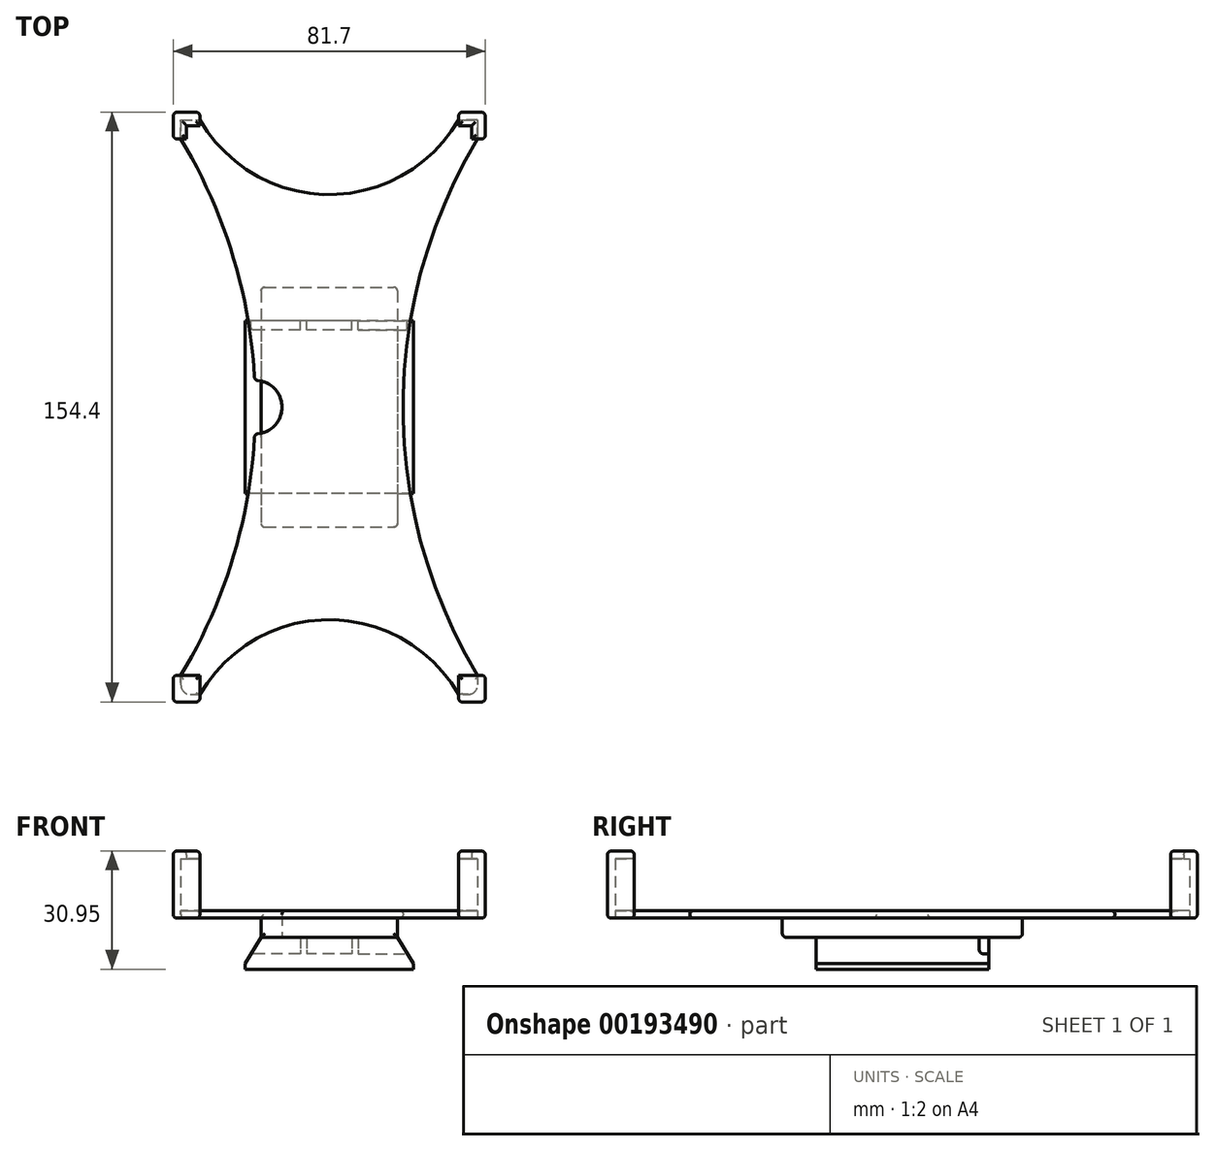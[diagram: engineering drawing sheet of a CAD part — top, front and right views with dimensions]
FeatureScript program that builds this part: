
annotation { "Feature Type Name" : "Feature", "Feature Type Description" : "" }
export const myFeature = defineFeature(function(context is Context, id is Id, definition is map)
    precondition{}
    {
        {
            var Q0;
            Q0=qCreatedBy(makeId("Top.planeOp"),FACE);
            var sketch = newSketch(context, id + "F0", { "sketchPlane" : qUnion([Q0])});
            skLineSegment(sketch, "E0.bottom", {"start": v(-38.85, 75.2) * mm, "end": v(-33.85, 75.2) * mm});
            skLineSegment(sketch, "E0.top", {"start": v(-38.85, -75.2) * mm, "end": v(-33.85, -75.2) * mm});
            skLineSegment(sketch, "E0.left", {"start": v(-38.85, 75.2) * mm, "end": v(-38.85, 70.2) * mm});
            skLineSegment(sketch, "E0.right", {"start": v(38.85, 75.2) * mm, "end": v(38.85, 70.2) * mm});
            skLineSegment(sketch, "E1", {"start": v(-38.85, 75.2) * mm, "end": v(38.85, -75.2) * mm, "construction": true});
            skArc(sketch, "E2", {"start": v(-33.85, 75.2) * mm, "mid": v(0, 55.65) * mm, "end": v(33.85, 75.2) * mm});
            skArc(sketch, "E3", {"start": v(-38.85, -70.2) * mm, "mid": v(-25.3, -39.79) * mm, "end": v(-19.53, -7) * mm});
            skArc(sketch, "E4.MirrorCS", {"start": v(38.85, -70.2) * mm, "mid": v(19.35, 0) * mm, "end": v(38.85, 70.2) * mm});
            skArc(sketch, "E5.MirrorCS", {"start": v(-33.85, -75.2) * mm, "mid": v(0, -55.65) * mm, "end": v(33.85, -75.2) * mm});
            skArc(sketch, "E6", {"start": v(-19.53, -7) * mm, "mid": v(-12.35, 0) * mm, "end": v(-19.53, 7) * mm});
            skArc(sketch, "E7.trimOffspring", {"start": v(-19.53, 7) * mm, "mid": v(-25.3, 39.79) * mm, "end": v(-38.85, 70.2) * mm});
            skLineSegment(sketch, "E8.bottom", {"start": v(-25.25, 66.5) * mm, "end": v(25.25, 66.5) * mm, "construction": true});
            skLineSegment(sketch, "E8.top", {"start": v(-25.25, 64.9) * mm, "end": v(25.25, 64.9) * mm, "construction": true});
            skLineSegment(sketch, "E8.left", {"start": v(-25.25, 66.5) * mm, "end": v(-25.25, 64.9) * mm, "construction": true});
            skLineSegment(sketch, "E8.right", {"start": v(25.25, 66.5) * mm, "end": v(25.25, 64.9) * mm, "construction": true});
            skLineSegment(sketch, "E9.trimOffspring", {"start": v(33.85, 75.2) * mm, "end": v(38.85, 75.2) * mm});
            skLineSegment(sketch, "E10.trimOffspring", {"start": v(-38.85, -70.2) * mm, "end": v(-38.85, -75.2) * mm});
            skLineSegment(sketch, "E11.trimOffspring", {"start": v(38.85, -70.2) * mm, "end": v(38.85, -75.2) * mm});
            skLineSegment(sketch, "E12.trimOffspring", {"start": v(33.85, -75.2) * mm, "end": v(38.85, -75.2) * mm});
            skSolve(sketch);
        }
        {
            var Q0;
            Q0 = qSketchRegion(id + "F0", true);
            extrude(context, id + "F1", {"entities" : qUnion([Q0]), "depth" : 2 * mm});
        }
        {
            var Q0;
            Q0=qCreatedBy(makeId("Top.planeOp"),FACE);
            var sketch = newSketch(context, id + "F2", { "sketchPlane" : qUnion([Q0])});
            skLineSegment(sketch, "E13", {"start": v(-33.85, 75.2) * mm, "end": v(-33.85, 77.2) * mm});
            skLineSegment(sketch, "E14", {"start": v(-33.85, 77.2) * mm, "end": v(-40.85, 77.2) * mm});
            skLineSegment(sketch, "E15", {"start": v(-40.85, 77.2) * mm, "end": v(-40.85, 70.2) * mm});
            skLineSegment(sketch, "E16", {"start": v(-40.85, 70.2) * mm, "end": v(-38.85, 70.2) * mm});
            skLineSegment(sketch, "E17", {"start": v(-38.85, 70.2) * mm, "end": v(-38.85, 75.2) * mm});
            skLineSegment(sketch, "E18", {"start": v(-38.85, 75.2) * mm, "end": v(-33.85, 75.2) * mm});
            skLineSegment(sketch, "E19.MirrorCS", {"start": v(40.85, 77.2) * mm, "end": v(40.85, 70.2) * mm});
            skLineSegment(sketch, "E20.MirrorCS", {"start": v(33.85, 77.2) * mm, "end": v(40.85, 77.2) * mm});
            skLineSegment(sketch, "E21.MirrorCS", {"start": v(40.85, 70.2) * mm, "end": v(38.85, 70.2) * mm});
            skLineSegment(sketch, "E22.MirrorCS", {"start": v(38.85, 75.2) * mm, "end": v(33.85, 75.2) * mm});
            skLineSegment(sketch, "E23.MirrorCS", {"start": v(38.85, 70.2) * mm, "end": v(38.85, 75.2) * mm});
            skLineSegment(sketch, "E24.MirrorCS", {"start": v(33.85, 75.2) * mm, "end": v(33.85, 77.2) * mm});
            skLineSegment(sketch, "E25.MirrorCS", {"start": v(33.85, -75.2) * mm, "end": v(33.85, -77.2) * mm});
            skLineSegment(sketch, "E26.MirrorCS", {"start": v(40.85, -70.2) * mm, "end": v(38.85, -70.2) * mm});
            skLineSegment(sketch, "E27.MirrorCS", {"start": v(-33.85, -75.2) * mm, "end": v(-33.85, -77.2) * mm});
            skLineSegment(sketch, "E28.MirrorCS", {"start": v(-40.85, -70.2) * mm, "end": v(-38.85, -70.2) * mm});
            skLineSegment(sketch, "E29.MirrorCS", {"start": v(38.85, -70.2) * mm, "end": v(38.85, -75.2) * mm});
            skLineSegment(sketch, "E30.MirrorCS", {"start": v(38.85, -75.2) * mm, "end": v(33.85, -75.2) * mm});
            skLineSegment(sketch, "E31.MirrorCS", {"start": v(33.85, -77.2) * mm, "end": v(40.85, -77.2) * mm});
            skLineSegment(sketch, "E32.MirrorCS", {"start": v(40.85, -77.2) * mm, "end": v(40.85, -70.2) * mm});
            skLineSegment(sketch, "E33.MirrorCS", {"start": v(-38.85, -75.2) * mm, "end": v(-33.85, -75.2) * mm});
            skLineSegment(sketch, "E34.MirrorCS", {"start": v(-38.85, -70.2) * mm, "end": v(-38.85, -75.2) * mm});
            skLineSegment(sketch, "E35.MirrorCS", {"start": v(-33.85, -77.2) * mm, "end": v(-40.85, -77.2) * mm});
            skLineSegment(sketch, "E36.MirrorCS", {"start": v(-40.85, -77.2) * mm, "end": v(-40.85, -70.2) * mm});
            skSolve(sketch);
        }
        {
            var Q0;
            Q0 = qSketchRegion(id + "F2", true);
            extrude(context, id + "F3", {"entities" : qUnion([Q0]), "operationType" : NewBodyOperationType.ADD, "depth" : (13.6 + 2) * mm});
        }
        {
            var Q0;
            Q0=makeQuery(id+"F3.opExtrude","CAP_FACE",FACE,{"disambiguationData":[OSD([sQuery(id+"F2.wireOp",EDGE,"E13"),sQuery(id+"F2.wireOp",EDGE,"E14"),sQuery(id+"F2.wireOp",EDGE,"E15"),sQuery(id+"F2.wireOp",EDGE,"E16"),sQuery(id+"F2.wireOp",EDGE,"E17"),sQuery(id+"F2.wireOp",EDGE,"E18")])],"isStart":false});
            var sketch = newSketch(context, id + "F4", { "sketchPlane" : qUnion([Q0])});
            skLineSegment(sketch, "E37.bottom", {"start": v(-40.85, -77.2) * mm, "end": v(-33.85, -77.2) * mm});
            skLineSegment(sketch, "E37.top", {"start": v(-40.85, -70.2) * mm, "end": v(-33.85, -70.2) * mm});
            skLineSegment(sketch, "E37.left", {"start": v(-40.85, -77.2) * mm, "end": v(-40.85, -70.2) * mm});
            skLineSegment(sketch, "E37.right", {"start": v(-33.85, -77.2) * mm, "end": v(-33.85, -70.2) * mm});
            skLineSegment(sketch, "E38", {"start": v(-40.85, 77.2) * mm, "end": v(-33.85, 77.2) * mm});
            skLineSegment(sketch, "E39", {"start": v(-33.85, 77.2) * mm, "end": v(-33.85, 73.7) * mm});
            skLineSegment(sketch, "E40", {"start": v(-33.85, 73.7) * mm, "end": v(-37.35, 73.7) * mm});
            skLineSegment(sketch, "E41", {"start": v(-37.35, 73.7) * mm, "end": v(-37.35, 70.2) * mm});
            skLineSegment(sketch, "E42", {"start": v(-37.35, 70.2) * mm, "end": v(-40.85, 70.2) * mm});
            skLineSegment(sketch, "E43", {"start": v(-40.85, 70.2) * mm, "end": v(-40.85, 77.2) * mm});
            skLineSegment(sketch, "E44.MirrorCS", {"start": v(33.85, 77.2) * mm, "end": v(33.85, 73.7) * mm});
            skLineSegment(sketch, "E45.MirrorCS", {"start": v(37.35, 70.2) * mm, "end": v(40.85, 70.2) * mm});
            skLineSegment(sketch, "E46.MirrorCS", {"start": v(33.85, 73.7) * mm, "end": v(37.35, 73.7) * mm});
            skLineSegment(sketch, "E47.MirrorCS", {"start": v(37.35, 73.7) * mm, "end": v(37.35, 70.2) * mm});
            skLineSegment(sketch, "E48.MirrorCS", {"start": v(40.85, -77.2) * mm, "end": v(40.85, -70.2) * mm});
            skLineSegment(sketch, "E49.MirrorCS", {"start": v(40.85, -70.2) * mm, "end": v(33.85, -70.2) * mm});
            skLineSegment(sketch, "E50.MirrorCS", {"start": v(40.85, 70.2) * mm, "end": v(40.85, 77.2) * mm});
            skLineSegment(sketch, "E51.MirrorCS", {"start": v(40.85, -77.2) * mm, "end": v(33.85, -77.2) * mm});
            skLineSegment(sketch, "E52.MirrorCS", {"start": v(40.85, 77.2) * mm, "end": v(33.85, 77.2) * mm});
            skLineSegment(sketch, "E53.MirrorCS", {"start": v(33.85, -77.2) * mm, "end": v(33.85, -70.2) * mm});
            skSolve(sketch);
        }
        {
            var Q0;
            Q0 = qSketchRegion(id + "F4", true);
            extrude(context, id + "F5", {"entities" : qUnion([Q0]), "operationType" : NewBodyOperationType.ADD, "depth" : 2 * mm});
        }
        {
            var Q0;
            Q0=qCreatedBy(makeId("Top.planeOp"),FACE);
            var sketch = newSketch(context, id + "F6", { "sketchPlane" : qUnion([Q0])});
            skLineSegment(sketch, "E54.bottom", {"start": v(-17.85, 31.43) * mm, "end": v(17.85, 31.43) * mm});
            skLineSegment(sketch, "E54.top", {"start": v(-17.85, -31.42) * mm, "end": v(17.85, -31.42) * mm});
            skLineSegment(sketch, "E54.left", {"start": v(-17.85, 31.43) * mm, "end": v(-17.85, 6.84) * mm});
            skLineSegment(sketch, "E54.right", {"start": v(17.85, 31.43) * mm, "end": v(17.85, -31.42) * mm});
            skLineSegment(sketch, "E55", {"start": v(-17.85, 31.43) * mm, "end": v(17.85, -31.43) * mm, "construction": true});
            skArc(sketch, "E56", {"start": v(-17.85, -6.84) * mm, "mid": v(-12.35, 0) * mm, "end": v(-17.85, 6.84) * mm});
            skLineSegment(sketch, "E57.trimOffspring", {"start": v(-17.85, -6.84) * mm, "end": v(-17.85, -31.42) * mm});
            skSolve(sketch);
        }
        {
            var Q0;
            Q0 = qSketchRegion(id + "F6", true);
            extrude(context, id + "F7", {"entities" : qUnion([Q0]), "operationType" : NewBodyOperationType.ADD, "oppositeDirection" : true, "depth" : 5 * mm});
        }
        {
            var Q0;
            Q0=makeQuery(id+"F7.opExtrude","CAP_FACE",FACE,{"disambiguationData":[OSD([sQuery(id+"F6.wireOp",EDGE,"E54.bottom"),sQuery(id+"F6.wireOp",EDGE,"E54.top"),sQuery(id+"F6.wireOp",EDGE,"E54.left"),sQuery(id+"F6.wireOp",EDGE,"E54.right"),sQuery(id+"F6.wireOp",EDGE,"E56"),sQuery(id+"F6.wireOp",EDGE,"E57.trimOffspring")])],"isStart":false});
            var sketch = newSketch(context, id + "F8", { "sketchPlane" : qUnion([Q0])});
            skLineSegment(sketch, "E58.bottom", {"start": v(17.85, -22.62) * mm, "end": v(-17.85, -22.62) * mm});
            skLineSegment(sketch, "E58.top", {"start": v(17.85, 22.62) * mm, "end": v(-17.85, 22.62) * mm});
            skLineSegment(sketch, "E58.left", {"start": v(17.85, -22.62) * mm, "end": v(17.85, 22.62) * mm});
            skLineSegment(sketch, "E58.right", {"start": v(-17.85, -22.62) * mm, "end": v(-17.85, 22.62) * mm});
            skPoint(sketch, "E58.middle", {"position": v(0, 0) * mm});
            skSolve(sketch);
        }
        {
            var Q0;
            {var subQ2=sQuery(id+"F8.wireOp",EDGE,"E58.bottom");Q0=makeQuery(id+"F8.imprint","IMPRINT",FACE,{"disambiguationData":[TD([[makeQuery(id+"F8.imprint","IMPRINT",EDGE,{"derivedFrom":subQ2}),-1.0]])]});}
            cPlane(context, id + "F9", {"entities" : qUnion([Q0]), "cplaneType" : CPlaneType.OFFSET, "offset" : 6.85 * mm, "width" : 150 * mm, "height" : 150 * mm});
        }
        {
            var Q0;
            Q0=qCreatedBy(id+"F9.planeOp",FACE);
            var sketch = newSketch(context, id + "F10", { "sketchPlane" : qUnion([Q0])});
            skLineSegment(sketch, "E59.bottom", {"start": v(22, -22.62) * mm, "end": v(-22, -22.62) * mm});
            skLineSegment(sketch, "E59.top", {"start": v(22, 22.62) * mm, "end": v(-22, 22.62) * mm});
            skLineSegment(sketch, "E59.left", {"start": v(22, -22.62) * mm, "end": v(22, 22.62) * mm});
            skLineSegment(sketch, "E59.right", {"start": v(-22, -22.62) * mm, "end": v(-22, 22.62) * mm});
            skPoint(sketch, "E59.middle", {"position": v(0, 0) * mm});
            skSolve(sketch);
        }
        {
            var Q1;
            Q1 = qSketchRegion(id + "F8", true);
            var Q2;
            Q2 = qSketchRegion(id + "F10", true);
            var Q3;
            Q3=sQuery(id+"F8.wireOp",VERTEX,"E58.right.end");
            var Q4;
            Q4=sQuery(id+"F10.wireOp",VERTEX,"E59.top.end");
            loft(context, id + "F11", {"operationType" : NewBodyOperationType.ADD, "sheetProfilesArray" : [{ "sheetProfileEntities" : qUnion([Q1]) }, { "sheetProfileEntities" : qUnion([Q2]) }], "matchConnections" : true, "connections" : [{ "connectionEntities" : qUnion([Q3, Q4]), "connectionEdgeQueries" : qUnion([]), "connectionEdgeParameters" : [] }]});
        }
        {
            var Q0;
            Q0 = qSketchRegion(id + "F10", true);
            extrude(context, id + "F12", {"entities" : qUnion([Q0]), "operationType" : NewBodyOperationType.ADD, "depth" : 1.5 * mm});
        }
        {
            var Q0;
            Q0=makeQuery(id+"F1.opExtrude","CAP_EDGE",EDGE,{"disambiguationData":[OSD([sQuery(id+"F0.wireOp",EDGE,"E2")])],"isStart":false});
            var Q1;
            Q1=makeQuery(id+"F1.opExtrude","CAP_EDGE",EDGE,{"disambiguationData":[OSD([sQuery(id+"F0.wireOp",EDGE,"E4.MirrorCS")])],"isStart":false});
            var Q2;
            Q2=makeQuery(id+"F1.opExtrude","CAP_EDGE",EDGE,{"disambiguationData":[OSD([sQuery(id+"F0.wireOp",EDGE,"E7.trimOffspring")])],"isStart":false});
            var Q3;
            Q3=makeQuery(id+"F1.opExtrude","CAP_EDGE",EDGE,{"disambiguationData":[OSD([sQuery(id+"F0.wireOp",EDGE,"E6")])],"isStart":false});
            var Q4;
            Q4=makeQuery(id+"F1.opExtrude","CAP_EDGE",EDGE,{"disambiguationData":[OSD([sQuery(id+"F0.wireOp",EDGE,"E3")])],"isStart":false});
            var Q5;
            Q5=makeQuery(id+"F1.opExtrude","CAP_EDGE",EDGE,{"disambiguationData":[OSD([sQuery(id+"F0.wireOp",EDGE,"E5.MirrorCS")])],"isStart":false});
            var Q6;
            Q6=makeQuery(id+"F1.opExtrude","SWEPT_EDGE",EDGE,{"disambiguationData":[OSD([sQuery(id+"F0.wireOp",EDGE,"E6"),sQuery(id+"F0.wireOp",EDGE,"E7.trimOffspring")])]});
            var Q7;
            Q7=makeQuery(id+"F1.opExtrude","CAP_EDGE",EDGE,{"disambiguationData":[OSD([sQuery(id+"F0.wireOp",EDGE,"E7.trimOffspring")])],"isStart":true});
            var Q8;
            Q8=makeQuery(id+"F1.opExtrude","CAP_EDGE",EDGE,{"disambiguationData":[OSD([sQuery(id+"F0.wireOp",EDGE,"E3")])],"isStart":true});
            var Q9;
            Q9=makeQuery(id+"F1.opExtrude","SWEPT_EDGE",EDGE,{"disambiguationData":[OSD([sQuery(id+"F0.wireOp",EDGE,"E3"),sQuery(id+"F0.wireOp",EDGE,"E6")])]});
            var Q10;
            {var subQ0=sQuery(id+"F0.wireOp",EDGE,"E6");var subQ1=sQuery(id+"F0.wireOp",EDGE,"E3");Q10=makeQuery(id+"F7.boolean.opBoolean","SPLIT",EDGE,{"disambiguationData":[TD([makeQuery(id+"F1.opExtrude","SWEPT_FACE",FACE,{"disambiguationData":[OSD([subQ1])]})])],"derivedFrom":makeQuery(id+"F1.opExtrude","CAP_EDGE",EDGE,{"disambiguationData":[OSD([subQ0])],"isStart":true})});}
            var Q11;
            {var subQ0=sQuery(id+"F0.wireOp",EDGE,"E7.trimOffspring");var subQ1=sQuery(id+"F0.wireOp",EDGE,"E6");Q11=makeQuery(id+"F7.boolean.opBoolean","SPLIT",EDGE,{"disambiguationData":[TD([makeQuery(id+"F1.opExtrude","SWEPT_FACE",FACE,{"disambiguationData":[OSD([subQ0])]})])],"derivedFrom":makeQuery(id+"F1.opExtrude","CAP_EDGE",EDGE,{"disambiguationData":[OSD([subQ1])],"isStart":true})});}
            var Q12;
            Q12=makeQuery(id+"F7.opExtrude","SWEPT_EDGE",EDGE,{"disambiguationData":[OSD([sQuery(id+"F6.wireOp",EDGE,"E54.left"),sQuery(id+"F6.wireOp",EDGE,"E56")])]});
            var Q13;
            Q13=makeQuery(id+"F7.opExtrude","SWEPT_EDGE",EDGE,{"disambiguationData":[OSD([sQuery(id+"F6.wireOp",EDGE,"E56"),sQuery(id+"F6.wireOp",EDGE,"E57.trimOffspring")])]});
            var Q14;
            Q14=makeQuery(id+"F1.opExtrude","CAP_EDGE",EDGE,{"disambiguationData":[OSD([sQuery(id+"F0.wireOp",EDGE,"E2")])],"isStart":true});
            var Q15;
            Q15=makeQuery(id+"F1.opExtrude","CAP_EDGE",EDGE,{"disambiguationData":[OSD([sQuery(id+"F0.wireOp",EDGE,"E4.MirrorCS")])],"isStart":true});
            var Q16;
            Q16=makeQuery(id+"F1.opExtrude","CAP_EDGE",EDGE,{"disambiguationData":[OSD([sQuery(id+"F0.wireOp",EDGE,"E5.MirrorCS")])],"isStart":true});
            var Q17;
            Q17=makeQuery(id+"F7.opExtrude","SWEPT_EDGE",EDGE,{"disambiguationData":[OSD([sQuery(id+"F6.wireOp",EDGE,"E54.bottom"),sQuery(id+"F6.wireOp",EDGE,"E54.right")])]});
            var Q18;
            Q18=makeQuery(id+"F7.opExtrude","SWEPT_EDGE",EDGE,{"disambiguationData":[OSD([sQuery(id+"F6.wireOp",EDGE,"E54.top"),sQuery(id+"F6.wireOp",EDGE,"E54.right")])]});
            var Q19;
            Q19=makeQuery(id+"F7.opExtrude","SWEPT_EDGE",EDGE,{"disambiguationData":[OSD([sQuery(id+"F6.wireOp",EDGE,"E54.top"),sQuery(id+"F6.wireOp",EDGE,"E57.trimOffspring")])]});
            var Q20;
            Q20=makeQuery(id+"F7.opExtrude","CAP_EDGE",EDGE,{"disambiguationData":[OSD([sQuery(id+"F6.wireOp",EDGE,"E54.bottom")])],"isStart":false});
            var Q21;
            Q21=makeQuery(id+"F7.opExtrude","SWEPT_EDGE",EDGE,{"disambiguationData":[OSD([sQuery(id+"F6.wireOp",EDGE,"E54.bottom"),sQuery(id+"F6.wireOp",EDGE,"E54.left")])]});
            var Q22;
            Q22=makeQuery(id+"F7.opExtrude","CAP_EDGE",EDGE,{"disambiguationData":[OSD([sQuery(id+"F6.wireOp",EDGE,"E54.top")])],"isStart":false});
            var Q23;
            Q23=makeQuery(id+"F5.opExtrude","CAP_FACE",FACE,{"disambiguationData":[OSD([sQuery(id+"F4.wireOp",EDGE,"E48.MirrorCS"),sQuery(id+"F4.wireOp",EDGE,"E49.MirrorCS"),sQuery(id+"F4.wireOp",EDGE,"E51.MirrorCS"),sQuery(id+"F4.wireOp",EDGE,"E53.MirrorCS")])],"isStart":false});
            var Q24;
            Q24=makeQuery(id+"F5.opExtrude","CAP_FACE",FACE,{"disambiguationData":[OSD([sQuery(id+"F4.wireOp",EDGE,"E37.bottom"),sQuery(id+"F4.wireOp",EDGE,"E37.top"),sQuery(id+"F4.wireOp",EDGE,"E37.left"),sQuery(id+"F4.wireOp",EDGE,"E37.right")])],"isStart":false});
            var Q25;
            Q25=makeQuery(id+"F5.boolean.opBoolean","MERGE",EDGE,{"derivedFrom":[makeQuery(id+"F3.opExtrude","SWEPT_EDGE",EDGE,{"disambiguationData":[OSD([sQuery(id+"F2.wireOp",EDGE,"E35.MirrorCS"),sQuery(id+"F2.wireOp",EDGE,"E36.MirrorCS")])]}),makeQuery(id+"F5.opExtrude","SWEPT_EDGE",EDGE,{"disambiguationData":[OSD([sQuery(id+"F4.wireOp",EDGE,"E37.bottom"),sQuery(id+"F4.wireOp",EDGE,"E37.left")])]})]});
            var Q26;
            Q26=makeQuery(id+"F5.boolean.opBoolean","MERGE",EDGE,{"derivedFrom":[makeQuery(id+"F3.opExtrude","SWEPT_EDGE",EDGE,{"disambiguationData":[OSD([sQuery(id+"F2.wireOp",EDGE,"E31.MirrorCS"),sQuery(id+"F2.wireOp",EDGE,"E32.MirrorCS")])]}),makeQuery(id+"F5.opExtrude","SWEPT_EDGE",EDGE,{"disambiguationData":[OSD([sQuery(id+"F4.wireOp",EDGE,"E48.MirrorCS"),sQuery(id+"F4.wireOp",EDGE,"E51.MirrorCS")])]})]});
            var Q27;
            Q27=makeQuery(id+"F3.opExtrude","CAP_EDGE",EDGE,{"disambiguationData":[OSD([sQuery(id+"F2.wireOp",EDGE,"E26.MirrorCS")])],"isStart":true});
            var Q28;
            Q28=makeQuery(id+"F3.opExtrude","CAP_EDGE",EDGE,{"disambiguationData":[OSD([sQuery(id+"F2.wireOp",EDGE,"E32.MirrorCS")])],"isStart":true});
            var Q29;
            Q29=makeQuery(id+"F3.opExtrude","CAP_EDGE",EDGE,{"disambiguationData":[OSD([sQuery(id+"F2.wireOp",EDGE,"E31.MirrorCS")])],"isStart":true});
            var Q30;
            Q30=makeQuery(id+"F3.opExtrude","CAP_EDGE",EDGE,{"disambiguationData":[OSD([sQuery(id+"F2.wireOp",EDGE,"E25.MirrorCS")])],"isStart":true});
            var Q31;
            Q31=makeQuery(id+"F3.opExtrude","CAP_EDGE",EDGE,{"disambiguationData":[OSD([sQuery(id+"F2.wireOp",EDGE,"E27.MirrorCS")])],"isStart":true});
            var Q32;
            Q32=makeQuery(id+"F3.opExtrude","CAP_EDGE",EDGE,{"disambiguationData":[OSD([sQuery(id+"F2.wireOp",EDGE,"E35.MirrorCS")])],"isStart":true});
            var Q33;
            Q33=makeQuery(id+"F3.opExtrude","CAP_EDGE",EDGE,{"disambiguationData":[OSD([sQuery(id+"F2.wireOp",EDGE,"E36.MirrorCS")])],"isStart":true});
            var Q34;
            Q34=makeQuery(id+"F3.opExtrude","CAP_EDGE",EDGE,{"disambiguationData":[OSD([sQuery(id+"F2.wireOp",EDGE,"E28.MirrorCS")])],"isStart":true});
            var Q35;
            Q35=makeQuery(id+"F5.opExtrude","CAP_FACE",FACE,{"disambiguationData":[OSD([sQuery(id+"F4.wireOp",EDGE,"E38"),sQuery(id+"F4.wireOp",EDGE,"E39"),sQuery(id+"F4.wireOp",EDGE,"E40"),sQuery(id+"F4.wireOp",EDGE,"E41"),sQuery(id+"F4.wireOp",EDGE,"E42"),sQuery(id+"F4.wireOp",EDGE,"E43")])],"isStart":false});
            var Q36;
            Q36=makeQuery(id+"F5.opExtrude","CAP_FACE",FACE,{"disambiguationData":[OSD([sQuery(id+"F4.wireOp",EDGE,"E44.MirrorCS"),sQuery(id+"F4.wireOp",EDGE,"E45.MirrorCS"),sQuery(id+"F4.wireOp",EDGE,"E46.MirrorCS"),sQuery(id+"F4.wireOp",EDGE,"E47.MirrorCS"),sQuery(id+"F4.wireOp",EDGE,"E50.MirrorCS"),sQuery(id+"F4.wireOp",EDGE,"E52.MirrorCS")])],"isStart":false});
            var Q37;
            Q37=makeQuery(id+"F3.opExtrude","CAP_EDGE",EDGE,{"disambiguationData":[OSD([sQuery(id+"F2.wireOp",EDGE,"E16")])],"isStart":true});
            var Q38;
            Q38=makeQuery(id+"F3.opExtrude","CAP_EDGE",EDGE,{"disambiguationData":[OSD([sQuery(id+"F2.wireOp",EDGE,"E13")])],"isStart":true});
            var Q39;
            Q39=makeQuery(id+"F3.opExtrude","CAP_EDGE",EDGE,{"disambiguationData":[OSD([sQuery(id+"F2.wireOp",EDGE,"E14")])],"isStart":true});
            var Q40;
            Q40=makeQuery(id+"F3.opExtrude","CAP_EDGE",EDGE,{"disambiguationData":[OSD([sQuery(id+"F2.wireOp",EDGE,"E15")])],"isStart":true});
            var Q41;
            Q41=makeQuery(id+"F3.opExtrude","CAP_EDGE",EDGE,{"disambiguationData":[OSD([sQuery(id+"F2.wireOp",EDGE,"E21.MirrorCS")])],"isStart":true});
            var Q42;
            Q42=makeQuery(id+"F3.opExtrude","CAP_EDGE",EDGE,{"disambiguationData":[OSD([sQuery(id+"F2.wireOp",EDGE,"E24.MirrorCS")])],"isStart":true});
            var Q43;
            Q43=makeQuery(id+"F3.opExtrude","CAP_EDGE",EDGE,{"disambiguationData":[OSD([sQuery(id+"F2.wireOp",EDGE,"E20.MirrorCS")])],"isStart":true});
            var Q44;
            Q44=makeQuery(id+"F3.opExtrude","CAP_EDGE",EDGE,{"disambiguationData":[OSD([sQuery(id+"F2.wireOp",EDGE,"E19.MirrorCS")])],"isStart":true});
            var Q45;
            Q45=makeQuery(id+"F5.boolean.opBoolean","MERGE",EDGE,{"derivedFrom":[makeQuery(id+"F3.opExtrude","SWEPT_EDGE",EDGE,{"disambiguationData":[OSD([sQuery(id+"F2.wireOp",EDGE,"E20.MirrorCS"),sQuery(id+"F2.wireOp",EDGE,"E24.MirrorCS")])]}),makeQuery(id+"F5.opExtrude","SWEPT_EDGE",EDGE,{"disambiguationData":[OSD([sQuery(id+"F4.wireOp",EDGE,"E44.MirrorCS"),sQuery(id+"F4.wireOp",EDGE,"E52.MirrorCS")])]})]});
            var Q46;
            Q46=makeQuery(id+"F5.boolean.opBoolean","MERGE",EDGE,{"derivedFrom":[makeQuery(id+"F3.opExtrude","SWEPT_EDGE",EDGE,{"disambiguationData":[OSD([sQuery(id+"F2.wireOp",EDGE,"E19.MirrorCS"),sQuery(id+"F2.wireOp",EDGE,"E20.MirrorCS")])]}),makeQuery(id+"F5.opExtrude","SWEPT_EDGE",EDGE,{"disambiguationData":[OSD([sQuery(id+"F4.wireOp",EDGE,"E50.MirrorCS"),sQuery(id+"F4.wireOp",EDGE,"E52.MirrorCS")])]})]});
            var Q47;
            Q47=makeQuery(id+"F5.boolean.opBoolean","MERGE",EDGE,{"derivedFrom":[makeQuery(id+"F3.opExtrude","SWEPT_EDGE",EDGE,{"disambiguationData":[OSD([sQuery(id+"F2.wireOp",EDGE,"E14"),sQuery(id+"F2.wireOp",EDGE,"E15")])]}),makeQuery(id+"F5.opExtrude","SWEPT_EDGE",EDGE,{"disambiguationData":[OSD([sQuery(id+"F4.wireOp",EDGE,"E38"),sQuery(id+"F4.wireOp",EDGE,"E43")])]})]});
            var Q48;
            Q48=makeQuery(id+"F5.boolean.opBoolean","MERGE",EDGE,{"derivedFrom":[makeQuery(id+"F3.opExtrude","SWEPT_EDGE",EDGE,{"disambiguationData":[OSD([sQuery(id+"F2.wireOp",EDGE,"E15"),sQuery(id+"F2.wireOp",EDGE,"E16")])]}),makeQuery(id+"F5.opExtrude","SWEPT_EDGE",EDGE,{"disambiguationData":[OSD([sQuery(id+"F4.wireOp",EDGE,"E42"),sQuery(id+"F4.wireOp",EDGE,"E43")])]})]});
            var Q49;
            Q49=makeQuery(id+"F5.boolean.opBoolean","MERGE",EDGE,{"derivedFrom":[makeQuery(id+"F3.opExtrude","SWEPT_EDGE",EDGE,{"disambiguationData":[OSD([sQuery(id+"F2.wireOp",EDGE,"E13"),sQuery(id+"F2.wireOp",EDGE,"E14")])]}),makeQuery(id+"F5.opExtrude","SWEPT_EDGE",EDGE,{"disambiguationData":[OSD([sQuery(id+"F4.wireOp",EDGE,"E38"),sQuery(id+"F4.wireOp",EDGE,"E39")])]})]});
            var Q50;
            Q50=makeQuery(id+"F5.boolean.opBoolean","MERGE",EDGE,{"derivedFrom":[makeQuery(id+"F3.opExtrude","SWEPT_EDGE",EDGE,{"disambiguationData":[OSD([sQuery(id+"F2.wireOp",EDGE,"E19.MirrorCS"),sQuery(id+"F2.wireOp",EDGE,"E21.MirrorCS")])]}),makeQuery(id+"F5.opExtrude","SWEPT_EDGE",EDGE,{"disambiguationData":[OSD([sQuery(id+"F4.wireOp",EDGE,"E45.MirrorCS"),sQuery(id+"F4.wireOp",EDGE,"E50.MirrorCS")])]})]});
            var Q51;
            Q51=makeQuery(id+"F5.boolean.opBoolean","MERGE",EDGE,{"derivedFrom":[makeQuery(id+"F3.opExtrude","SWEPT_EDGE",EDGE,{"disambiguationData":[OSD([sQuery(id+"F2.wireOp",EDGE,"E26.MirrorCS"),sQuery(id+"F2.wireOp",EDGE,"E32.MirrorCS")])]}),makeQuery(id+"F5.opExtrude","SWEPT_EDGE",EDGE,{"disambiguationData":[OSD([sQuery(id+"F4.wireOp",EDGE,"E48.MirrorCS"),sQuery(id+"F4.wireOp",EDGE,"E49.MirrorCS")])]})]});
            var Q52;
            Q52=makeQuery(id+"F5.boolean.opBoolean","MERGE",EDGE,{"derivedFrom":[makeQuery(id+"F3.opExtrude","SWEPT_EDGE",EDGE,{"disambiguationData":[OSD([sQuery(id+"F2.wireOp",EDGE,"E25.MirrorCS"),sQuery(id+"F2.wireOp",EDGE,"E31.MirrorCS")])]}),makeQuery(id+"F5.opExtrude","SWEPT_EDGE",EDGE,{"disambiguationData":[OSD([sQuery(id+"F4.wireOp",EDGE,"E51.MirrorCS"),sQuery(id+"F4.wireOp",EDGE,"E53.MirrorCS")])]})]});
            var Q53;
            Q53=makeQuery(id+"F5.boolean.opBoolean","MERGE",EDGE,{"derivedFrom":[makeQuery(id+"F3.opExtrude","SWEPT_EDGE",EDGE,{"disambiguationData":[OSD([sQuery(id+"F2.wireOp",EDGE,"E27.MirrorCS"),sQuery(id+"F2.wireOp",EDGE,"E35.MirrorCS")])]}),makeQuery(id+"F5.opExtrude","SWEPT_EDGE",EDGE,{"disambiguationData":[OSD([sQuery(id+"F4.wireOp",EDGE,"E37.bottom"),sQuery(id+"F4.wireOp",EDGE,"E37.right")])]})]});
            var Q54;
            Q54=makeQuery(id+"F5.boolean.opBoolean","MERGE",EDGE,{"derivedFrom":[makeQuery(id+"F3.opExtrude","SWEPT_EDGE",EDGE,{"disambiguationData":[OSD([sQuery(id+"F2.wireOp",EDGE,"E28.MirrorCS"),sQuery(id+"F2.wireOp",EDGE,"E36.MirrorCS")])]}),makeQuery(id+"F5.opExtrude","SWEPT_EDGE",EDGE,{"disambiguationData":[OSD([sQuery(id+"F4.wireOp",EDGE,"E37.top"),sQuery(id+"F4.wireOp",EDGE,"E37.left")])]})]});
            fillet(context, id + "F13", {"entities" : qUnion([Q0, Q1, Q2, Q3, Q4, Q5, Q6, Q7, Q8, Q9, Q10, Q11, Q12, Q13, Q14, Q15, Q16, Q17, Q18, Q19, Q20, Q21, Q22, Q23, Q24, Q25, Q26, Q27, Q28, Q29, Q30, Q31, Q32, Q33, Q34, Q35, Q36, Q37, Q38, Q39, Q40, Q41, Q42, Q43, Q44, Q45, Q46, Q47, Q48, Q49, Q50, Q51, Q52, Q53, Q54]), "radius" : 1 * mm, "tangentPropagation" : true, "allowEdgeOverflow" : false});
        }
        {
            var Q0;
            Q0=makeQuery(id+"F1.opExtrude","CAP_EDGE",EDGE,{"disambiguationData":[OSD([sQuery(id+"F0.wireOp",EDGE,"E11.trimOffspring")])],"isStart":false});
            var Q1;
            Q1=makeQuery(id+"F1.opExtrude","CAP_EDGE",EDGE,{"disambiguationData":[OSD([sQuery(id+"F0.wireOp",EDGE,"E12.trimOffspring")])],"isStart":false});
            var Q2;
            Q2=makeQuery(id+"F3.opExtrude","SWEPT_EDGE",EDGE,{"disambiguationData":[OSD([sQuery(id+"F2.wireOp",EDGE,"E29.MirrorCS"),sQuery(id+"F2.wireOp",EDGE,"E30.MirrorCS")])]});
            var Q3;
            Q3=makeQuery(id+"F3.opExtrude","CAP_EDGE",EDGE,{"disambiguationData":[OSD([sQuery(id+"F2.wireOp",EDGE,"E30.MirrorCS")])],"isStart":false});
            var Q4;
            Q4=makeQuery(id+"F3.opExtrude","CAP_EDGE",EDGE,{"disambiguationData":[OSD([sQuery(id+"F2.wireOp",EDGE,"E29.MirrorCS")])],"isStart":false});
            var Q5;
            Q5=makeQuery(id+"F3.opExtrude","SWEPT_EDGE",EDGE,{"disambiguationData":[OSD([sQuery(id+"F2.wireOp",EDGE,"E33.MirrorCS"),sQuery(id+"F2.wireOp",EDGE,"E34.MirrorCS")])]});
            var Q6;
            Q6=makeQuery(id+"F1.opExtrude","CAP_EDGE",EDGE,{"disambiguationData":[OSD([sQuery(id+"F0.wireOp",EDGE,"E0.top")])],"isStart":false});
            var Q7;
            Q7=makeQuery(id+"F1.opExtrude","CAP_EDGE",EDGE,{"disambiguationData":[OSD([sQuery(id+"F0.wireOp",EDGE,"E10.trimOffspring")])],"isStart":false});
            var Q8;
            Q8=makeQuery(id+"F3.opExtrude","CAP_EDGE",EDGE,{"disambiguationData":[OSD([sQuery(id+"F2.wireOp",EDGE,"E33.MirrorCS")])],"isStart":false});
            var Q9;
            Q9=makeQuery(id+"F3.opExtrude","CAP_EDGE",EDGE,{"disambiguationData":[OSD([sQuery(id+"F2.wireOp",EDGE,"E34.MirrorCS")])],"isStart":false});
            var Q10;
            Q10=makeQuery(id+"F3.opExtrude","CAP_EDGE",EDGE,{"disambiguationData":[OSD([sQuery(id+"F2.wireOp",EDGE,"E17")])],"isStart":false});
            var Q11;
            Q11=makeQuery(id+"F1.opExtrude","CAP_EDGE",EDGE,{"disambiguationData":[OSD([sQuery(id+"F0.wireOp",EDGE,"E0.left")])],"isStart":false});
            var Q12;
            Q12=makeQuery(id+"F1.opExtrude","CAP_EDGE",EDGE,{"disambiguationData":[OSD([sQuery(id+"F0.wireOp",EDGE,"E0.right")])],"isStart":false});
            var Q13;
            Q13=makeQuery(id+"F3.opExtrude","CAP_EDGE",EDGE,{"disambiguationData":[OSD([sQuery(id+"F2.wireOp",EDGE,"E23.MirrorCS")])],"isStart":false});
            fillet(context, id + "F14", {"entities" : qUnion([Q0, Q1, Q2, Q3, Q4, Q5, Q6, Q7, Q8, Q9, Q10, Q11, Q12, Q13]), "radius" : 2.5 * mm, "tangentPropagation" : true, "allowEdgeOverflow" : false});
        }
        {
            var Q0;
            {var subQ0=sQuery(id+"F10.wireOp",EDGE,"E59.bottom");Q0=makeQuery(id+"F12.boolean.opBoolean","MERGE",FACE,{"derivedFrom":[makeQuery(id+"F11.opLoft","SWEPT_FACE",FACE,{"disambiguationData":[OSD([sQuery(id+"F6.wireOp",EDGE,"E54.left"),sQuery(id+"F6.wireOp",EDGE,"E54.right"),sQuery(id+"F8.wireOp",EDGE,"E58.bottom"),sQuery(id+"F8.wireOp",EDGE,"E58.left"),sQuery(id+"F8.wireOp",EDGE,"E58.right"),subQ0,sQuery(id+"F10.wireOp",EDGE,"E59.left"),sQuery(id+"F10.wireOp",EDGE,"E59.right")])]}),makeQuery(id+"F12.opExtrude","SWEPT_FACE",FACE,{"disambiguationData":[OSD([subQ0])]})]});}
            var sketch = newSketch(context, id + "F15", { "sketchPlane" : qUnion([Q0])});
            skLineSegment(sketch, "E60", {"start": v(0, -5) * mm, "end": v(-5.9, -5) * mm});
            skLineSegment(sketch, "E61", {"start": v(-5.9, -5) * mm, "end": v(-5.9, -9.3) * mm});
            skLineSegment(sketch, "E62", {"start": v(-5.9, -9.3) * mm, "end": v(0, -9.3) * mm});
            skLineSegment(sketch, "E63", {"start": v(-17.85, -5) * mm, "end": v(-7.6, -5) * mm});
            skLineSegment(sketch, "E64", {"start": v(-7.6, -5) * mm, "end": v(-7.6, -9.3) * mm});
            skLineSegment(sketch, "E65", {"start": v(-7.6, -9.3) * mm, "end": v(-20.46, -9.3) * mm});
            skLineSegment(sketch, "E66", {"start": v(-20.46, -9.3) * mm, "end": v(-17.85, -5) * mm});
            skLineSegment(sketch, "E67.MirrorCS", {"start": v(7.6, -5) * mm, "end": v(7.6, -9.3) * mm});
            skLineSegment(sketch, "E68.MirrorCS", {"start": v(17.85, -5) * mm, "end": v(7.6, -5) * mm});
            skLineSegment(sketch, "E69.MirrorCS", {"start": v(20.46, -9.3) * mm, "end": v(17.85, -5) * mm});
            skLineSegment(sketch, "E70.MirrorCS", {"start": v(5.9, -9.3) * mm, "end": v(0, -9.3) * mm});
            skLineSegment(sketch, "E71.MirrorCS", {"start": v(5.9, -5) * mm, "end": v(5.9, -9.3) * mm});
            skLineSegment(sketch, "E72.MirrorCS", {"start": v(0, -5) * mm, "end": v(5.9, -5) * mm});
            skLineSegment(sketch, "E73.MirrorCS", {"start": v(7.6, -9.3) * mm, "end": v(20.46, -9.3) * mm});
            skSolve(sketch);
        }
        {
            var Q0;
            Q0 = qSketchRegion(id + "F15", true);
            extrude(context, id + "F16", {"entities" : qUnion([Q0]), "operationType" : NewBodyOperationType.REMOVE, "oppositeDirection" : true, "depth" : 2.5 * mm});
        }
        {
            var Q0;
            Q0=makeQuery(id+"F16.boolean.opBoolean","COPY",EDGE,{"derivedFrom":makeQuery(id+"F16.opExtrude","CAP_EDGE",EDGE,{"disambiguationData":[OSD([sQuery(id+"F15.wireOp",EDGE,"E65")])],"isStart":false})});
            var Q1;
            Q1=makeQuery(id+"F16.boolean.opBoolean","COPY",EDGE,{"derivedFrom":makeQuery(id+"F16.opExtrude","CAP_EDGE",EDGE,{"disambiguationData":[OSD([sQuery(id+"F15.wireOp",EDGE,"E62"),sQuery(id+"F15.wireOp",EDGE,"E70.MirrorCS")])],"isStart":false})});
            var Q2;
            Q2=makeQuery(id+"F16.boolean.opBoolean","COPY",EDGE,{"derivedFrom":makeQuery(id+"F16.opExtrude","CAP_EDGE",EDGE,{"disambiguationData":[OSD([sQuery(id+"F15.wireOp",EDGE,"E73.MirrorCS")])],"isStart":false})});
            fillet(context, id + "F17", {"entities" : qUnion([Q0, Q1, Q2]), "radius" : 1 * mm, "tangentPropagation" : true, "allowEdgeOverflow" : false});
        }
    });
